# Revit family: Bath-Drop_In-BubbleMassage-KOHLER-SERIF-K-1337T_1
name_source: partatom
category: Plumbing Fixtures
revit_build: Autodesk Revit 2017 (Build: 20160225_1515(x64)
units: mm (PartAtom-declared; Revit-internal decimal feet)

## family parameters
Cut with Voids When Loaded = No
Host = Face
OmniClass Number = 23.31.15.00
OmniClass Title = Bathtubs
Part Type = Normal
Room Calculation Point = No
Round Connector Dimension = Use Diameter
Shared = No

## types (2) — shared parameters
ADA Compliant = No
Amplifer Electrical Connector = Amplifer Electrical Connector
Apparent Load = 1224 VA
Assembly Code = D2010500
Blower Electrical Connector = Blower Electrical Connector
CW Connection = No
Cold Water Inlet = Cold Water Inlet
Date Modified = 06/07/2021
Default Elevation = 0"
Drain Included = No
Electrical Connector = Yes
Electrical Note = One dedicated circuit required
Finish = KOHLER-Acrylic-0-White
HW Connection = No
Heater Electrical Connector = Heater Electrical Connector
Height = 24"
Hot Water Inlet = Hot Water Inlet
Length = 60"
Manufacturer = KOHLER Co.
Master Format 2014 = 22 41 19
Master Format 2014 Name = Residential Bathtubs
Material = High brightness acrylic
Product Documentation Link = https://files.kohler.com.cn
Product Name = SERIF
Product Page URL = https://www.kohler.com.cn
Pump Electrical Connector = Pump Electrical Connector
Vent Connection = No
Voltage = 240 V
Waste Connection = Yes
Waste Water Outlet = Waste Water Outlet
WaterSense Certified = No
Width = 42 1/4"

## per-type parameters (varying)
| type | Description | Drain Location | Electrical connector Location | Left Hand Drain | Model | Right Hand Drain | Type | URL |
| Left Hand Drain, 0-White | SERIF BUBBLEMASSAGE BATH, L/DRAIN | 11" | 56 7/8" | Yes | K-1337T-G1-0 | No | 1 | https://www.kohler.com.cn |
| Right Hand Drain, 0-White | SERIF BUBBLEMASSAGE BATH, R/DRAIN | 49" | 3 1/8" | No | K-1337T-G2-0 | Yes | 2 | https://www.us.kohler.com |

## geometry (parser evidence)
native form markers: Sweep x6
no freeform markers — native parametric forms only
